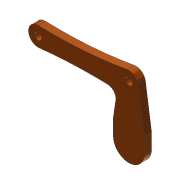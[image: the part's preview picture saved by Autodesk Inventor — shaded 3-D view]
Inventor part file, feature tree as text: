
AUTODESK INVENTOR PART (.ipt)
format: ipt  version: 2019.4 (Build 234330000, 330)  size: 143,360 bytes
history: native  units: mm
features: extrude x2, other x1, hole x1, sketch x1
ambient origin geometry x8: Origin, YZ Plane, XZ Plane, XY Plane, X Axis, Y Axis, Z Axis, Center Point
bodies: Body1 (feature_tree)
feature tree (5):
  other  "ソリッド1"
  extrude  "押し出し1"  Depth=20.0mm
  hole  "穴1"  [1 undecoded]
  extrude  "押し出し2"  Depth=4.0mm
  sketch  "スケッチ2"
note: 1 required parameter value undecoded (feature->parameter linkage not recoverable at this tier; creation-order binding heuristic only, values carry confidence <= 0.55)
